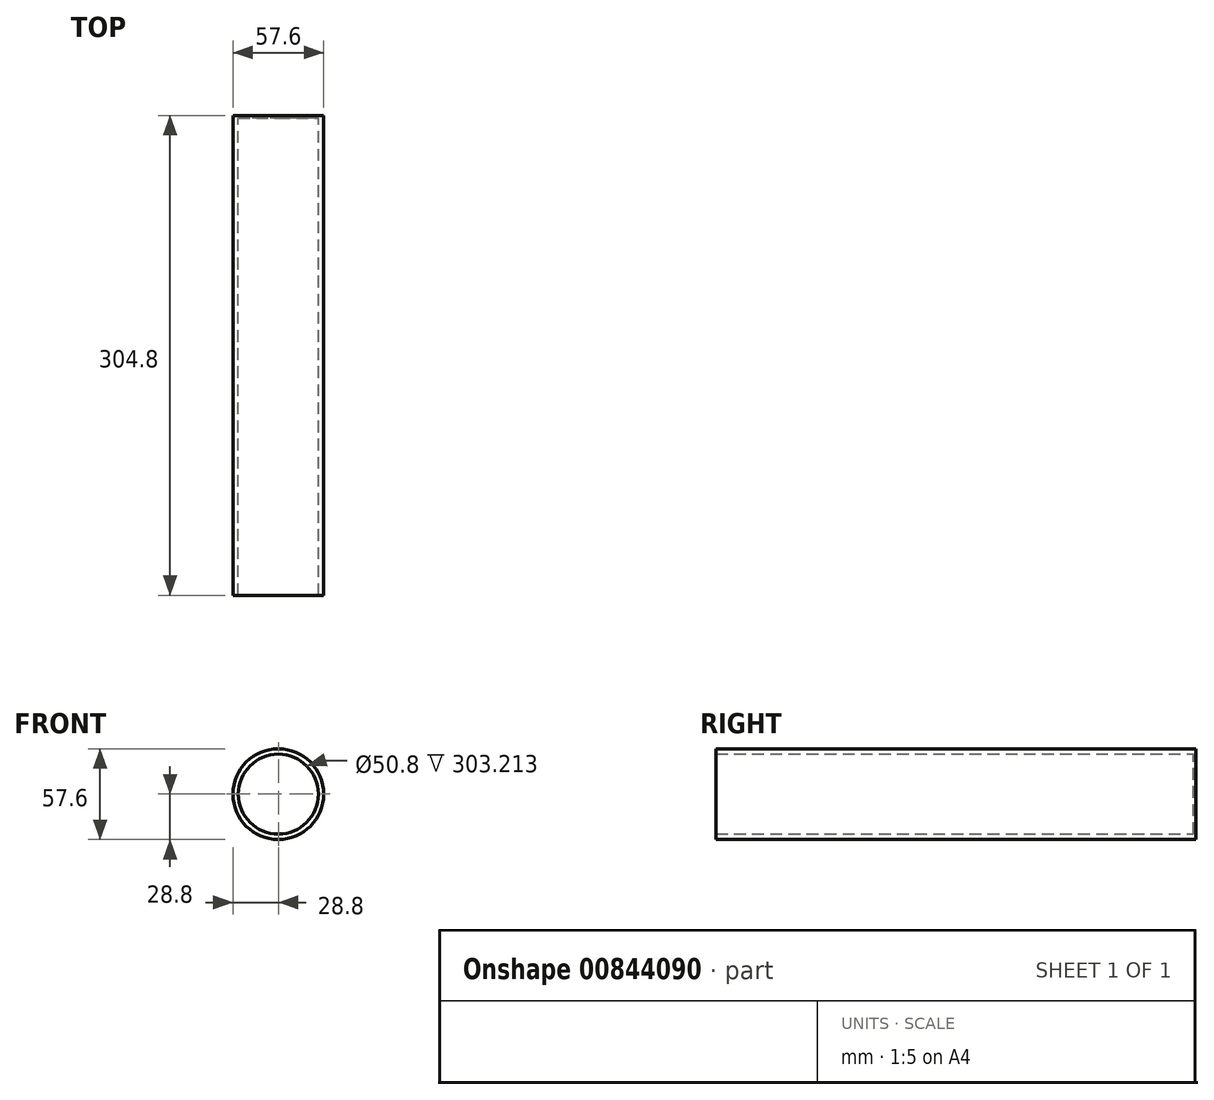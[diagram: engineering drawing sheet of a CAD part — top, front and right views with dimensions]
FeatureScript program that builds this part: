
annotation { "Feature Type Name" : "Feature", "Feature Type Description" : "" }
export const myFeature = defineFeature(function(context is Context, id is Id, definition is map)
    precondition{}
    {
        {
            var Q0;
            Q0=qCreatedBy(makeId("Front.planeOp"),FACE);
            var sketch = newSketch(context, id + "F0", { "sketchPlane" : qUnion([Q0])});
            skCircle(sketch, "E0", {"center": v(0, 0) * mm, "radius": 28.8 * mm});
            skCircle(sketch, "E1", {"center": v(0, 0) * mm, "radius": 25.4 * mm});
            skSolve(sketch);
        }
        {
            var Q0;
            Q0=makeQuery(id+"F0.imprint","IMPRINT",FACE,{"disambiguationData":[TD([[makeQuery(id+"F0.imprint","IMPRINT",EDGE,{"derivedFrom":sQuery(id+"F0.wireOp",EDGE,"E0")}),1.0]])]});
            extrude(context, id + "F1", {"entities" : qUnion([Q0]), "depth" : 304.8 * mm, "offsetDistance" : 25.4 * mm});
        }
        {
            var Q0;
            Q0=qCreatedBy(makeId("Front.planeOp"),FACE);
            cPlane(context, id + "F2", {"entities" : qUnion([Q0]), "cplaneType" : CPlaneType.OFFSET, "offset" : 60.96 * mm, "width" : 152.4 * mm, "height" : 152.4 * mm});
        }
        {
            var Q0;
            Q0=qCreatedBy(id+"F2.planeOp",FACE);
            cPlane(context, id + "F3", {"entities" : qUnion([Q0]), "cplaneType" : CPlaneType.OFFSET, "offset" : 60.96 * mm, "width" : 152.4 * mm, "height" : 152.4 * mm});
        }
        {
            var Q0;
            Q0=qCreatedBy(id+"F3.planeOp",FACE);
            cPlane(context, id + "F4", {"entities" : qUnion([Q0]), "cplaneType" : CPlaneType.OFFSET, "offset" : 60.96 * mm, "width" : 152.4 * mm, "height" : 152.4 * mm});
        }
        {
            var Q0;
            Q0=qCreatedBy(id+"F4.planeOp",FACE);
            cPlane(context, id + "F5", {"entities" : qUnion([Q0]), "cplaneType" : CPlaneType.OFFSET, "offset" : 60.96 * mm, "width" : 152.4 * mm, "height" : 152.4 * mm});
        }
        {
            var Q0;
            Q0=makeQuery(id+"F0.imprint","IMPRINT",FACE,{"disambiguationData":[TD([[makeQuery(id+"F0.imprint","IMPRINT",EDGE,{"derivedFrom":sQuery(id+"F0.wireOp",EDGE,"E1")}),1.0]])]});
            extrude(context, id + "F6", {"entities" : qUnion([Q0]), "operationType" : NewBodyOperationType.ADD, "depth" : 1.59 * mm, "offsetDistance" : 25.4 * mm});
        }
    });
